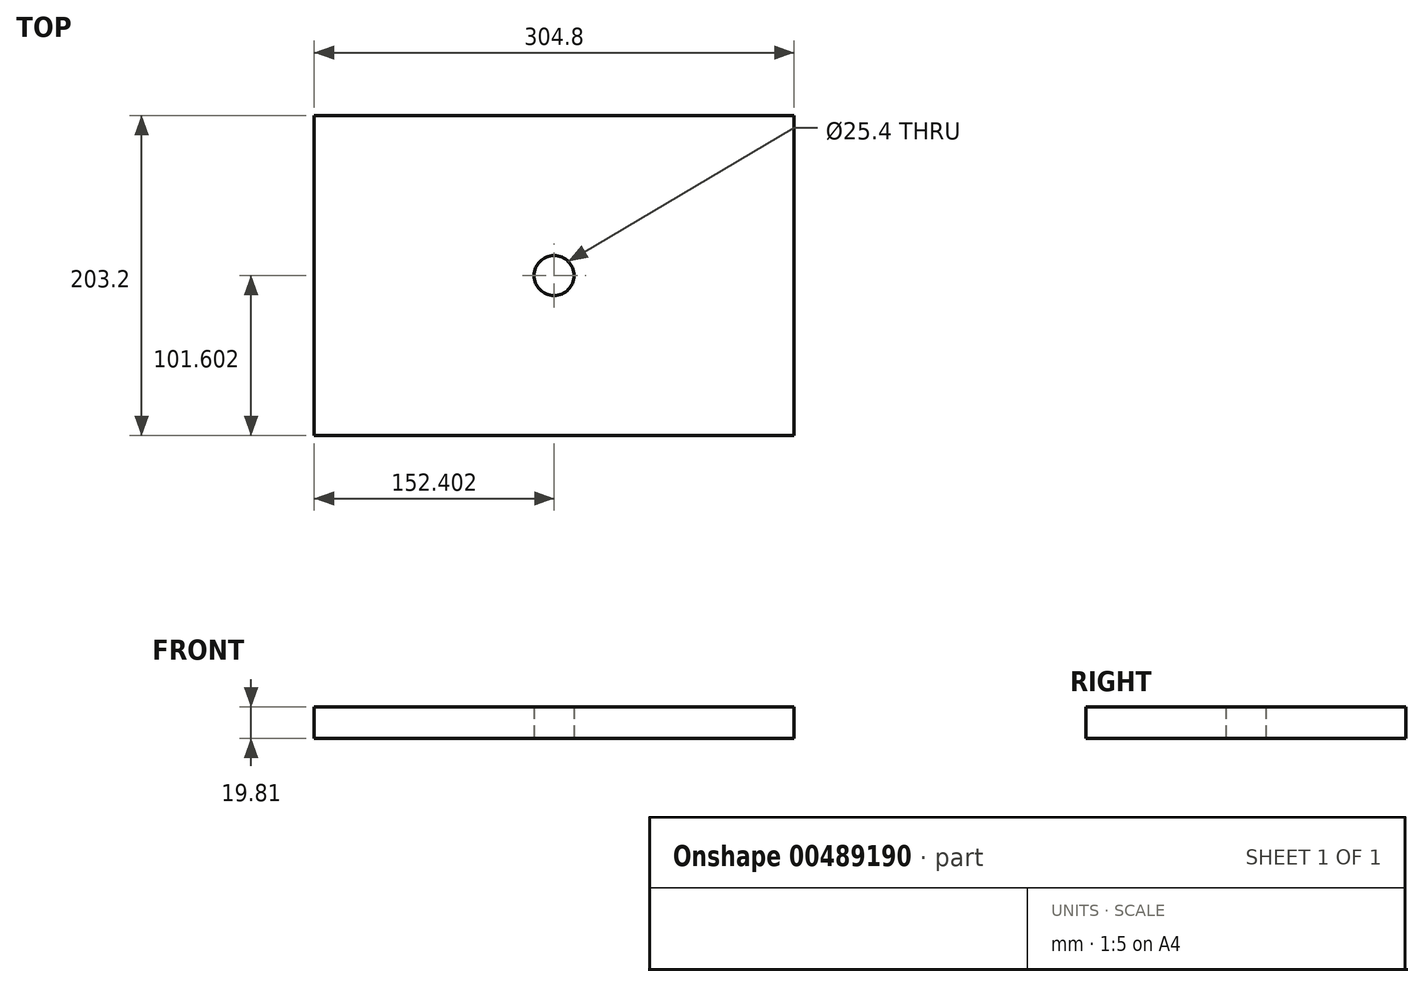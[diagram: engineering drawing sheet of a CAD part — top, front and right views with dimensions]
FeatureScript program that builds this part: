
annotation { "Feature Type Name" : "Feature", "Feature Type Description" : "" }
export const myFeature = defineFeature(function(context is Context, id is Id, definition is map)
    precondition{}
    {
        {
            var Q0;
            Q0=qCreatedBy(makeId("Top.planeOp"),FACE);
            var sketch = newSketch(context, id + "F0", { "sketchPlane" : qUnion([Q0])});
            skLineSegment(sketch, "E0.bottom", {"start": v(-190.56, 157.42) * mm, "end": v(114.24, 157.42) * mm});
            skLineSegment(sketch, "E0.top", {"start": v(-190.56, -45.78) * mm, "end": v(114.24, -45.78) * mm});
            skLineSegment(sketch, "E0.left", {"start": v(-190.56, 157.42) * mm, "end": v(-190.56, -45.78) * mm});
            skLineSegment(sketch, "E0.right", {"start": v(114.24, 157.42) * mm, "end": v(114.24, -45.78) * mm});
            skCircle(sketch, "E1", {"center": v(-38.16, 55.82) * mm, "radius": 12.7 * mm});
            skPoint(sketch, "E1.centerSnap0", {"position": v(114.24, 55.82) * mm});
            skPoint(sketch, "E1.centerSnap1", {"position": v(-38.16, 157.42) * mm});
            skSolve(sketch);
        }
        {
            var Q0;
            Q0=makeQuery(id+"F0.imprint","IMPRINT",FACE,{"disambiguationData":[TD([[makeQuery(id+"F0.imprint","IMPRINT",EDGE,{"derivedFrom":sQuery(id+"F0.wireOp",EDGE,"E0.bottom")}),-1.0]])]});
            extrude(context, id + "F1", {"entities" : qUnion([Q0]), "depth" : 19.8 * mm, "offsetDistance" : 25.4 * mm});
        }
    });
